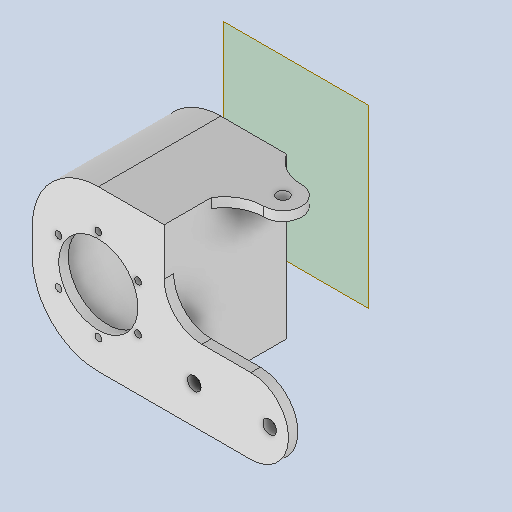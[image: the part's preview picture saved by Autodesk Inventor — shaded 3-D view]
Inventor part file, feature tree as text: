
AUTODESK INVENTOR PART (.ipt)
format: ipt  version: 2024 (Build 280153000, 153)  size: 582,656 bytes
history: native  units: in
note: dims shown in document units (in); Inventor stores cm internally (conversion verified against a paired STEP export)
features: extrude x5, sketch x5, projected_geometry x3, fillet x1, plane x1, mirror x1
ambient origin geometry x8: Origin, YZ Plane, XZ Plane, XY Plane, X Axis, Y Axis, Z Axis, Center Point
bodies: Solid1 (feature_tree)
feature tree (16):
  extrude  "Extrusion1"  Depth=2.0in
  extrude  "Extrusion2"  Depth=1.5in
  extrude  "Extrusion3"  Depth=0.09in
  extrude  "Extrusion4"  Depth=0.125in TaperAngle=0.0deg
  fillet  "Fillet2"  Radius=0.4in
  plane  "Work Plane1"
  mirror  "Mirror1"
  extrude  "Extrusion5"  Depth=0.125in
  sketch  "Sketch1"  dims[d1=1.5in d2=2.0in]
  sketch  "Sketch3"  dims[d3=1.5in d4=0.0in d6=1.05in]
  projected_geometry  "Projected Loop2"
  sketch  "Sketch4"  dims[d7=0.09in d8=0.61in]
  projected_geometry  "Projected Loop3"
  sketch  "Sketch6"  dims[d9=2.3622in d11=360.0deg d13=0.125in d14=0.0in d15=0.4in]
  projected_geometry  "Projected Loop5"
  sketch  "Sketch7"  dims[d16=1.0in d17=0.18in d18=1.0in d19=0.25in d20=0.125in d21=0.0in d22=1.75in d24=0.45in d25=0.16in d26=0.25in d27=0.25in d28=0.125in d29=0.0in d30=0.5in d32=0.125in d33=1.0in d34=0.0in d35=0.0in d36=1.0in d37=0.125in]
